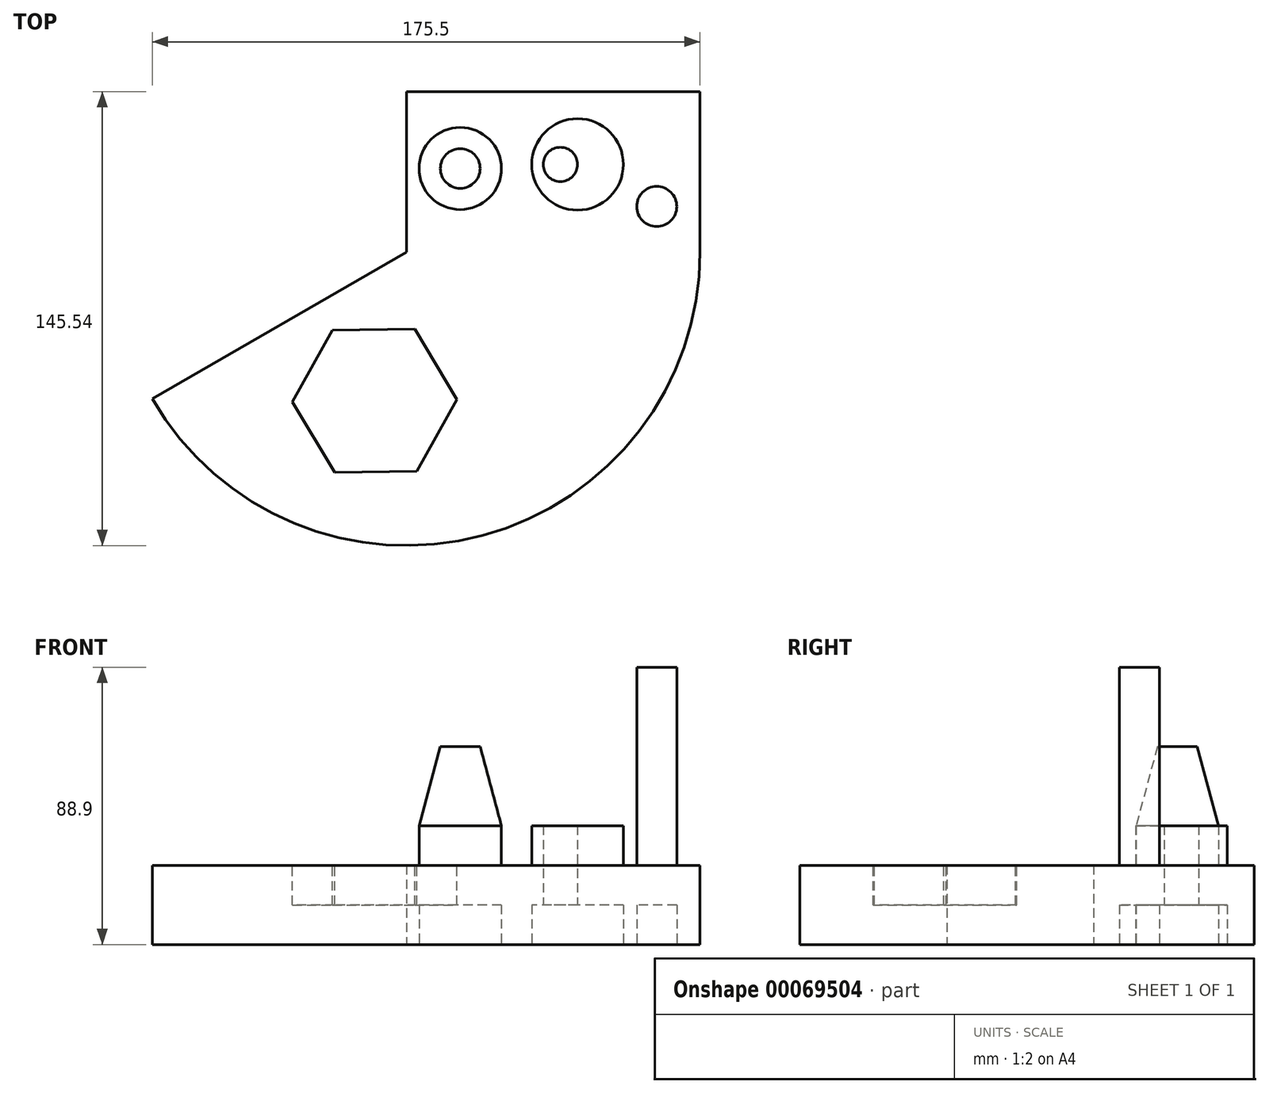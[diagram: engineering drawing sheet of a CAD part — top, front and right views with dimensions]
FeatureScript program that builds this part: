
annotation { "Feature Type Name" : "Feature", "Feature Type Description" : "" }
export const myFeature = defineFeature(function(context is Context, id is Id, definition is map)
    precondition{}
    {
        {
            var Q0;
            Q0=qCreatedBy(makeId("Top.planeOp"),FACE);
            var sketch = newSketch(context, id + "F0", { "sketchPlane" : qUnion([Q0])});
            skLineSegment(sketch, "E0.bottom", {"start": v(0, 0) * mm, "end": v(94.05, 0) * mm});
            skLineSegment(sketch, "E0.top", {"start": v(0, 51.49) * mm, "end": v(94.05, 51.49) * mm});
            skLineSegment(sketch, "E0.left", {"start": v(0, 0) * mm, "end": v(0, 51.49) * mm});
            skLineSegment(sketch, "E0.right", {"start": v(94.05, 0) * mm, "end": v(94.05, 51.49) * mm});
            skCircle(sketch, "E1", {"center": v(17.22, 26.82) * mm, "radius": 13.18 * mm});
            skCircle(sketch, "E2", {"center": v(54.8, 28.12) * mm, "radius": 14.67 * mm});
            skCircle(sketch, "E3", {"center": v(80.16, 14.63) * mm, "radius": 6.42 * mm});
            skCircle(sketch, "E4", {"center": v(49.3, 28.12) * mm, "radius": 5.5 * mm});
            skSolve(sketch);
        }
        {
            var Q0;
            Q0=makeQuery(id+"F0.imprint","IMPRINT",FACE,{"disambiguationData":[TD([[makeQuery(id+"F0.imprint","IMPRINT",EDGE,{"derivedFrom":sQuery(id+"F0.wireOp",EDGE,"E1")}),1.0]])]});
            var Q1;
            Q1=makeQuery(id+"F0.imprint","IMPRINT",FACE,{"disambiguationData":[TD([[makeQuery(id+"F0.imprint","IMPRINT",EDGE,{"derivedFrom":sQuery(id+"F0.wireOp",EDGE,"E2")}),1.0]])]});
            extrude(context, id + "F1", {"entities" : qUnion([Q0, Q1]), "depth" : 25.4 * mm});
        }
        {
            var Q0;
            Q0=makeQuery(id+"F0.imprint","IMPRINT",FACE,{"disambiguationData":[TD([[makeQuery(id+"F0.imprint","IMPRINT",EDGE,{"derivedFrom":sQuery(id+"F0.wireOp",EDGE,"E0.bottom")}),1.0]])]});
            extrude(context, id + "F2", {"entities" : qUnion([Q0]), "operationType" : NewBodyOperationType.ADD, "endBound" : BoundingType.SYMMETRIC, "depth" : 25.4 * mm});
        }
        {
            var Q0;
            Q0=makeQuery(id+"F0.imprint","IMPRINT",FACE,{"disambiguationData":[TD([[makeQuery(id+"F0.imprint","IMPRINT",EDGE,{"derivedFrom":sQuery(id+"F0.wireOp",EDGE,"E3")}),1.0]])]});
            extrude(context, id + "F3", {"entities" : qUnion([Q0]), "operationType" : NewBodyOperationType.ADD, "depth" : 76.2 * mm});
        }
        {
            var Q0;
            Q0=makeQuery(id+"F1.opExtrude","CAP_FACE",FACE,{"disambiguationData":[OSD([sQuery(id+"F0.wireOp",EDGE,"E1")])],"isStart":false});
            extrude(context, id + "F4", {"entities" : qUnion([Q0]), "operationType" : NewBodyOperationType.ADD, "depth" : 25.4 * mm, "hasDraft" : true, "draftAngle" : 15 * degree, "draftPullDirection" : true});
        }
        {
            var Q0;
            Q0=makeQuery(id+"F2.opExtrude","SWEPT_FACE",FACE,{"disambiguationData":[OSD([sQuery(id+"F0.wireOp",EDGE,"E0.bottom")])]});
            var Q1;
            Q1=makeQuery(id+"F2.opExtrude","SWEPT_EDGE",EDGE,{"disambiguationData":[OSD([sQuery(id+"F0.wireOp",EDGE,"E0.bottom"),sQuery(id+"F0.wireOp",EDGE,"E0.left")])]});
            revolve(context, id + "F5", {"operationType" : NewBodyOperationType.ADD, "entities" : qUnion([Q0]), "axis" : qUnion([Q1]), "revolveType" : RevolveType.ONE_DIRECTION, "angle" : 150 * degree});
        }
        {
            var Q0;
            {var subQ0=sQuery(id+"F0.wireOp",EDGE,"E0.bottom");Q0=makeQuery(id+"F5.boolean.opBoolean","MERGE",FACE,{"derivedFrom":[makeQuery(id+"F2.opExtrude","CAP_FACE",FACE,{"disambiguationData":[OSD([subQ0,sQuery(id+"F0.wireOp",EDGE,"E0.top"),sQuery(id+"F0.wireOp",EDGE,"E0.left"),sQuery(id+"F0.wireOp",EDGE,"E0.right"),sQuery(id+"F0.wireOp",EDGE,"E1"),sQuery(id+"F0.wireOp",EDGE,"E2"),sQuery(id+"F0.wireOp",EDGE,"E3")])],"isStart":false}),makeQuery(id+"F5.opRevolve","SWEPT_FACE",FACE,{"disambiguationData":[OSD([subQ0]),TDD([makeQuery(id+"F2.opExtrude","CAP_EDGE",EDGE,{"disambiguationData":[OSD([subQ0])],"isStart":false})])]})]});}
            var sketch = newSketch(context, id + "F6", { "sketchPlane" : qUnion([Q0])});
            skCircle(sketch, "E5.cCircle", {"center": v(-10.17, -47.61) * mm, "radius": 22.8 * mm, "construction": true});
            skLineSegment(sketch, "E5.0", {"start": v(2.63, -24.6) * mm, "end": v(16.17, -47.19) * mm});
            skLineSegment(sketch, "E5.1", {"start": v(16.17, -47.19) * mm, "end": v(3.37, -70.2) * mm});
            skLineSegment(sketch, "E5.2", {"start": v(3.37, -70.2) * mm, "end": v(-22.96, -70.63) * mm});
            skLineSegment(sketch, "E5.3", {"start": v(-22.96, -70.63) * mm, "end": v(-36.5, -48.04) * mm});
            skLineSegment(sketch, "E5.4", {"start": v(-36.5, -48.04) * mm, "end": v(-23.7, -25.02) * mm});
            skLineSegment(sketch, "E5.5", {"start": v(-23.7, -25.02) * mm, "end": v(2.63, -24.6) * mm});
            skPoint(sketch, "E5.0.midPoint", {"position": v(9.4, -35.9) * mm});
            skSolve(sketch);
        }
        {
            var Q0;
            Q0=makeQuery(id+"F6.imprint","IMPRINT",FACE,{"disambiguationData":[TD([[makeQuery(id+"F6.imprint","IMPRINT",EDGE,{"derivedFrom":sQuery(id+"F6.wireOp",EDGE,"E5.0")}),-1.0]])]});
            extrude(context, id + "F7", {"entities" : qUnion([Q0]), "operationType" : NewBodyOperationType.REMOVE, "oppositeDirection" : true, "depth" : 12.7 * mm});
        }
    });
